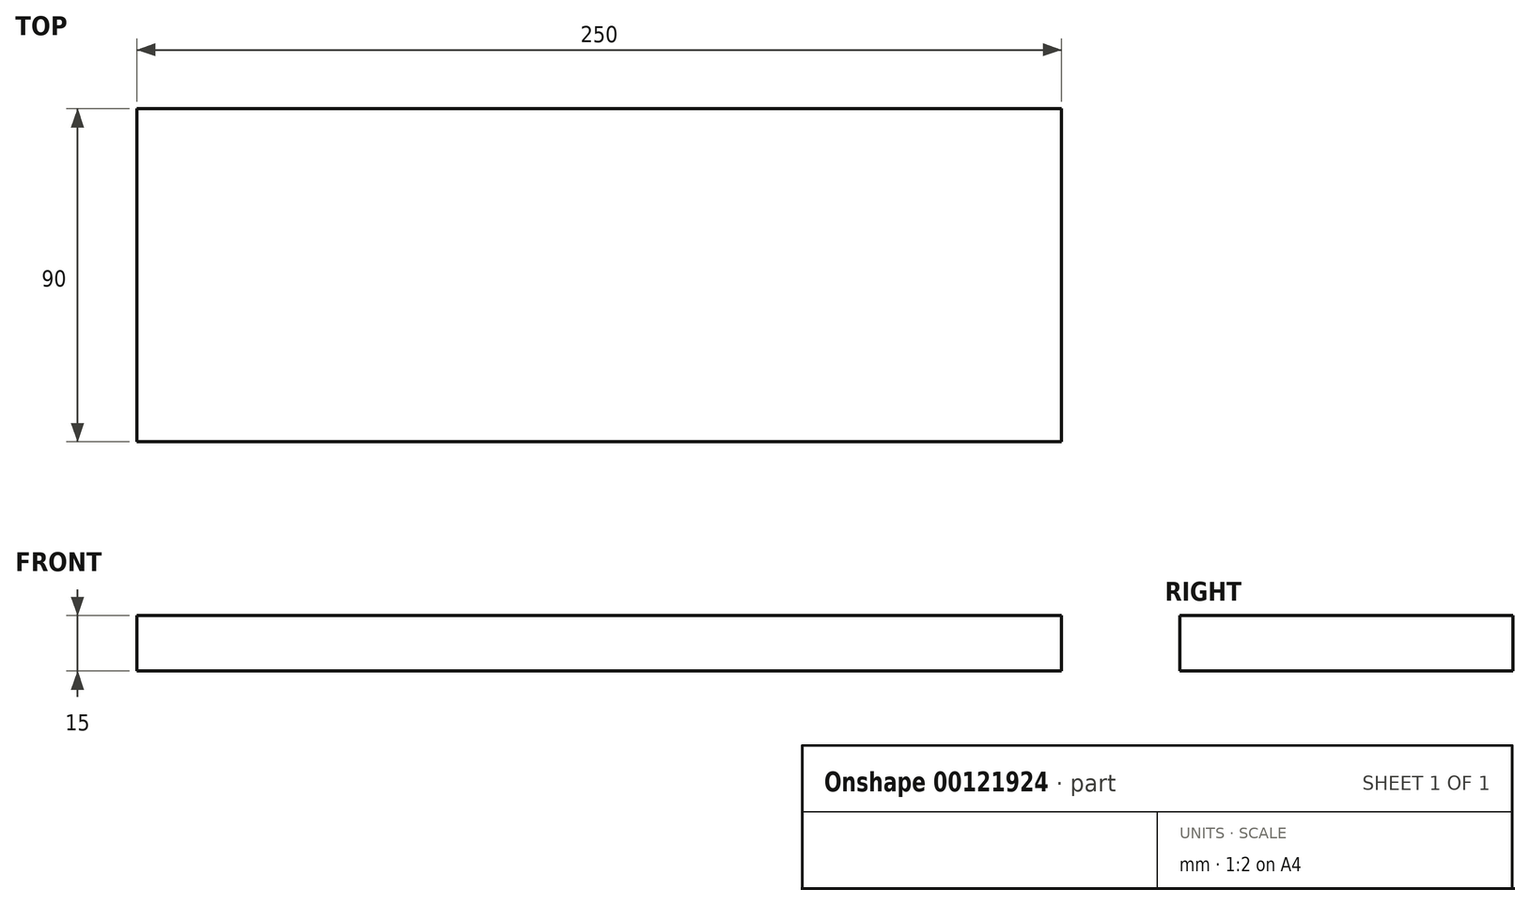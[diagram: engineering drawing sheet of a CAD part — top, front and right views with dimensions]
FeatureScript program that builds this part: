
annotation { "Feature Type Name" : "Feature", "Feature Type Description" : "" }
export const myFeature = defineFeature(function(context is Context, id is Id, definition is map)
    precondition{}
    {
        {
            var Q0;
            Q0=qCreatedBy(makeId("Top.planeOp"),FACE);
            var sketch = newSketch(context, id + "F0", { "sketchPlane" : qUnion([Q0])});
            skLineSegment(sketch, "E0.bottom", {"start": v(-125, -45) * mm, "end": v(125, -45) * mm});
            skLineSegment(sketch, "E0.top", {"start": v(-125, 45) * mm, "end": v(125, 45) * mm});
            skLineSegment(sketch, "E0.left", {"start": v(-125, -45) * mm, "end": v(-125, 45) * mm});
            skLineSegment(sketch, "E0.right", {"start": v(125, -45) * mm, "end": v(125, 45) * mm});
            skPoint(sketch, "E0.middle", {"position": v(0, 0) * mm});
            skSolve(sketch);
        }
        {
            var Q0;
            Q0=makeQuery(id+"F0.imprint","IMPRINT",FACE,{"disambiguationData":[TD([[makeQuery(id+"F0.imprint","IMPRINT",EDGE,{"derivedFrom":sQuery(id+"F0.wireOp",EDGE,"E0.bottom")}),1.0]])]});
            extrude(context, id + "F1", {"entities" : qUnion([Q0]), "depth" : 15 * mm});
        }
    });
